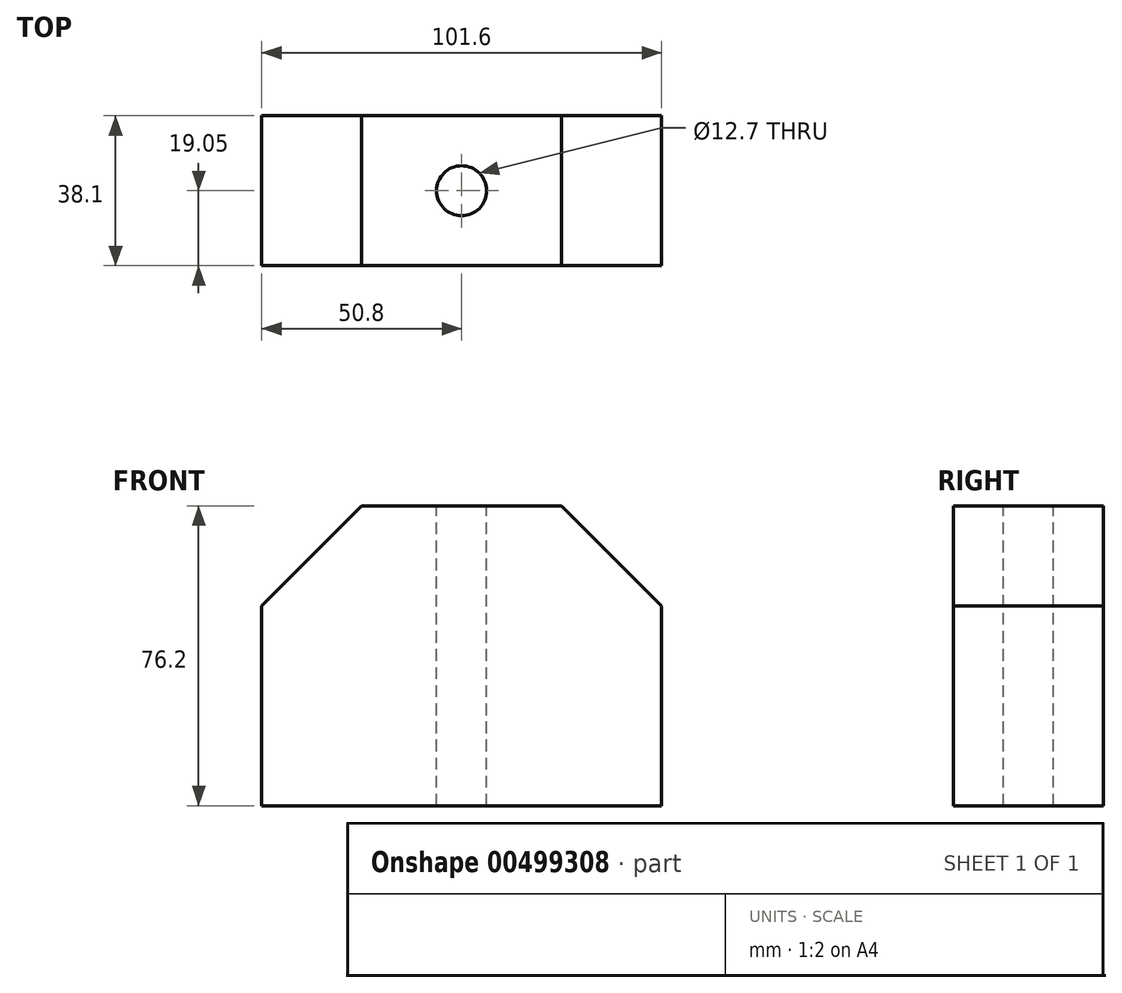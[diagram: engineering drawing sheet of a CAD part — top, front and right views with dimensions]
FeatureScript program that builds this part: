
annotation { "Feature Type Name" : "Feature", "Feature Type Description" : "" }
export const myFeature = defineFeature(function(context is Context, id is Id, definition is map)
    precondition{}
    {
        {
            var Q0;
            Q0=qCreatedBy(makeId("Front.planeOp"),FACE);
            var sketch = newSketch(context, id + "F0", { "sketchPlane" : qUnion([Q0])});
            skLineSegment(sketch, "E0", {"start": v(0, 0) * mm, "end": v(101.6, 0) * mm});
            skLineSegment(sketch, "E1", {"start": v(101.6, 0) * mm, "end": v(101.6, 50.8) * mm});
            skLineSegment(sketch, "E2", {"start": v(101.6, 50.8) * mm, "end": v(76.2, 76.2) * mm});
            skLineSegment(sketch, "E3", {"start": v(76.2, 76.2) * mm, "end": v(25.4, 76.2) * mm});
            skLineSegment(sketch, "E4", {"start": v(25.4, 76.2) * mm, "end": v(0, 50.8) * mm});
            skLineSegment(sketch, "E5", {"start": v(0, 50.8) * mm, "end": v(0, 0) * mm});
            skSolve(sketch);
        }
        {
            var Q0;
            Q0=makeQuery(id+"F0.imprint","IMPRINT",FACE,{"disambiguationData":[TD([[makeQuery(id+"F0.imprint","IMPRINT",EDGE,{"derivedFrom":sQuery(id+"F0.wireOp",EDGE,"E0")}),1.0]])]});
            extrude(context, id + "F1", {"entities" : qUnion([Q0]), "depth" : 38.1 * mm});
        }
        {
            var Q0;
            Q0=makeQuery(id+"F1.opExtrude","SWEPT_FACE",FACE,{"disambiguationData":[OSD([sQuery(id+"F0.wireOp",EDGE,"E3")])]});
            var sketch = newSketch(context, id + "F2", { "sketchPlane" : qUnion([Q0])});
            skLineSegment(sketch, "E6", {"start": v(50.8, -38.1) * mm, "end": v(50.8, -19.05) * mm});
            skCircle(sketch, "E7", {"center": v(50.8, -19.05) * mm, "radius": 6.35 * mm});
            skSolve(sketch);
        }
        {
            var Q0;
            Q0=makeQuery(id+"F2.imprint","IMPRINT",FACE,{"disambiguationData":[TD([[makeQuery(id+"F2.imprint","IMPRINT",EDGE,{"derivedFrom":sQuery(id+"F2.wireOp",EDGE,"E7")}),1.0]])]});
            extrude(context, id + "F3", {"entities" : qUnion([Q0]), "operationType" : NewBodyOperationType.REMOVE, "endBound" : BoundingType.THROUGH_ALL, "oppositeDirection" : true, "depth" : 25.4 * mm});
        }
    });
